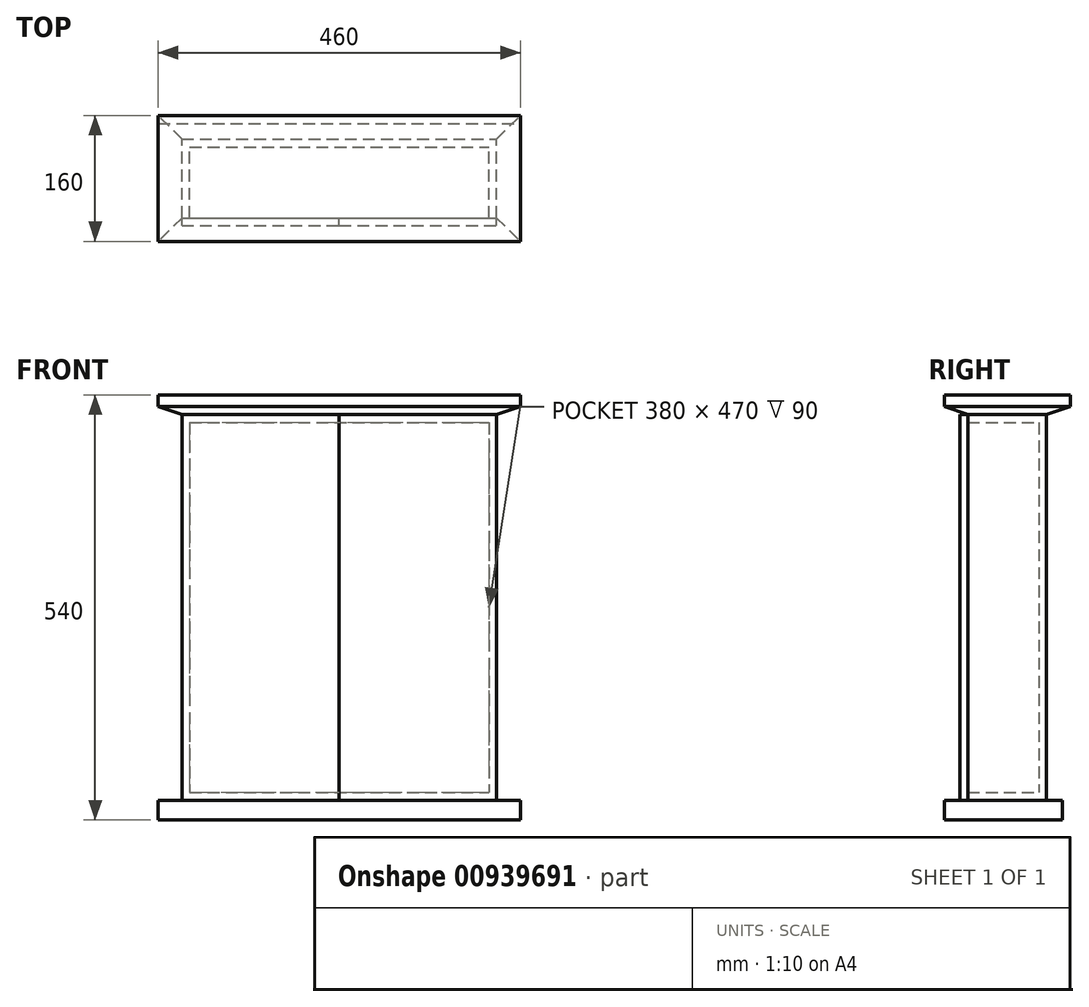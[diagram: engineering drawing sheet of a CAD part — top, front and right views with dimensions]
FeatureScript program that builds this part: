
annotation { "Feature Type Name" : "Feature", "Feature Type Description" : "" }
export const myFeature = defineFeature(function(context is Context, id is Id, definition is map)
    precondition{}
    {
        {
            var Q0;
            Q0=qCreatedBy(makeId("Front.planeOp"),FACE);
            var sketch = newSketch(context, id + "F0", { "sketchPlane" : qUnion([Q0])});
            skLineSegment(sketch, "E0.bottom", {"start": v(-200, 336.12) * mm, "end": v(200, 336.12) * mm});
            skLineSegment(sketch, "E0.top", {"start": v(-200, -153.88) * mm, "end": v(200, -153.88) * mm});
            skLineSegment(sketch, "E0.left", {"start": v(-200, 336.12) * mm, "end": v(-200, -153.88) * mm});
            skLineSegment(sketch, "E0.right", {"start": v(200, 336.12) * mm, "end": v(200, -153.88) * mm});
            skSolve(sketch);
        }
        {
            var Q0;
            Q0 = qSketchRegion(id + "F0", true);
            extrude(context, id + "F1", {"entities" : qUnion([Q0]), "depth" : 100 * mm, "offsetDistance" : 25 * mm});
        }
        {
            var Q0;
            Q0=makeQuery(id+"F1.opExtrude","CAP_FACE",FACE,{"disambiguationData":[OSD([sQuery(id+"F0.wireOp",EDGE,"E0.bottom"),sQuery(id+"F0.wireOp",EDGE,"E0.top"),sQuery(id+"F0.wireOp",EDGE,"E0.left"),sQuery(id+"F0.wireOp",EDGE,"E0.right")])],"isStart":false});
            shell(context, id + "F2", {"entities" : qUnion([Q0]), "thickness" : 10 * mm});
        }
        {
            var Q0;
            Q0=makeQuery(id+"F1.opExtrude","SWEPT_FACE",FACE,{"disambiguationData":[OSD([sQuery(id+"F0.wireOp",EDGE,"E0.bottom")])]});
            var sketch = newSketch(context, id + "F3", { "sketchPlane" : qUnion([Q0])});
            skLineSegment(sketch, "E1.bottom", {"start": v(-230, 30) * mm, "end": v(230, 30) * mm});
            skLineSegment(sketch, "E1.top", {"start": v(-230, -130) * mm, "end": v(230, -130) * mm});
            skLineSegment(sketch, "E1.left", {"start": v(-230, 30) * mm, "end": v(-230, -130) * mm});
            skLineSegment(sketch, "E1.right", {"start": v(230, 30) * mm, "end": v(230, -130) * mm});
            skSolve(sketch);
        }
        {
            var Q0;
            Q0 = qSketchRegion(id + "F3", true);
            extrude(context, id + "F4", {"entities" : qUnion([Q0]), "depth" : 25 * mm, "offsetDistance" : 25 * mm, "hasSecondDirection" : true, "secondDirectionOppositeDirection" : false, "secondDirectionDepth" : 10 * mm});
        }
        {
            var Q1;
            Q1=makeQuery(id+"F1.opExtrude","SWEPT_FACE",FACE,{"disambiguationData":[OSD([sQuery(id+"F0.wireOp",EDGE,"E0.bottom")])]});
            var Q2;
            Q2=makeQuery(id+"F4.opExtrude","CAP_FACE",FACE,{"disambiguationData":[OSD([sQuery(id+"F3.wireOp",EDGE,"E1.bottom"),sQuery(id+"F3.wireOp",EDGE,"E1.top"),sQuery(id+"F3.wireOp",EDGE,"E1.left"),sQuery(id+"F3.wireOp",EDGE,"E1.right")])],"isStart":true});
            loft(context, id + "F5", {"operationType" : NewBodyOperationType.ADD, "sheetProfilesArray" : [{ "sheetProfileEntities" : qUnion([Q1]) }, { "sheetProfileEntities" : qUnion([Q2]) }]});
        }
        {
            var Q0;
            Q0=makeQuery(id+"F1.opExtrude","SWEPT_FACE",FACE,{"disambiguationData":[OSD([sQuery(id+"F0.wireOp",EDGE,"E0.top")])]});
            var sketch = newSketch(context, id + "F6", { "sketchPlane" : qUnion([Q0])});
            skLineSegment(sketch, "E2.bottom", {"start": v(-230, 130) * mm, "end": v(230, 130) * mm});
            skLineSegment(sketch, "E2.top", {"start": v(-230, -20) * mm, "end": v(230, -20) * mm});
            skLineSegment(sketch, "E2.left", {"start": v(-230, 130) * mm, "end": v(-230, -20) * mm});
            skLineSegment(sketch, "E2.right", {"start": v(230, 130) * mm, "end": v(230, -20) * mm});
            skSolve(sketch);
        }
        {
            var Q0;
            Q0=makeQuery(id+"F6.imprint","IMPRINT",FACE,{"disambiguationData":[TD([[makeQuery(id+"F6.imprint","IMPRINT",EDGE,{"derivedFrom":sQuery(id+"F6.wireOp",EDGE,"E2.bottom")}),-1.0]])]});
            var Q1;
            {var subQ0=sQuery(id+"F0.wireOp",EDGE,"E0.top");Q1=makeQuery(id+"F6.imprint","IMPRINT",FACE,{"disambiguationData":[TD([[makeQuery(id+"F6.imprint","IMPRINT",EDGE,{"derivedFrom":makeQuery(id+"F1.opExtrude","CAP_EDGE",EDGE,{"disambiguationData":[OSD([subQ0])],"isStart":true})}),1.0]])]});}
            extrude(context, id + "F7", {"entities" : qUnion([Q0, Q1]), "operationType" : NewBodyOperationType.ADD, "depth" : 25 * mm, "offsetDistance" : 25 * mm});
        }
        {
            var Q0;
            Q0=makeQuery(id+"F1.opExtrude","CAP_FACE",FACE,{"disambiguationData":[OSD([sQuery(id+"F0.wireOp",EDGE,"E0.bottom"),sQuery(id+"F0.wireOp",EDGE,"E0.top"),sQuery(id+"F0.wireOp",EDGE,"E0.left"),sQuery(id+"F0.wireOp",EDGE,"E0.right")])],"isStart":false});
            var sketch = newSketch(context, id + "F8", { "sketchPlane" : qUnion([Q0])});
            skLineSegment(sketch, "E3.bottom", {"start": v(0, 336.12) * mm, "end": v(200, 336.12) * mm});
            skLineSegment(sketch, "E3.top", {"start": v(0, -153.88) * mm, "end": v(200, -153.88) * mm});
            skLineSegment(sketch, "E3.left", {"start": v(0, 336.12) * mm, "end": v(0, -153.88) * mm});
            skLineSegment(sketch, "E3.right", {"start": v(200, 336.12) * mm, "end": v(200, -153.88) * mm});
            skLineSegment(sketch, "E4.bottom", {"start": v(0, 336.12) * mm, "end": v(-200, 336.12) * mm});
            skLineSegment(sketch, "E4.top", {"start": v(0, -153.88) * mm, "end": v(-200, -153.88) * mm});
            skLineSegment(sketch, "E4.right", {"start": v(-200, 336.12) * mm, "end": v(-200, -153.88) * mm});
            skSolve(sketch);
        }
        {
            var Q0;
            {var subQ7=sQuery(id+"F8.wireOp",EDGE,"E3.bottom");Q0=makeQuery(id+"F8.imprint","IMPRINT",FACE,{"disambiguationData":[TD([[makeQuery(id+"F8.imprint","IMPRINT",EDGE,{"derivedFrom":subQ7}),-1.0]])]});}
            var Q1;
            {var subQ7=sQuery(id+"F0.wireOp",EDGE,"E0.right");var subQ8=makeQuery(id+"F2.opShell","OFFSET_EDGE",EDGE,{"disambiguationData":[OSD([subQ7]),TDD([makeQuery(id+"F1.opExtrude","CAP_EDGE",EDGE,{"disambiguationData":[OSD([subQ7])],"isStart":false})])]});Q1=makeQuery(id+"F8.imprint","IMPRINT",FACE,{"disambiguationData":[TD([[makeQuery(id+"F8.imprint","IMPRINT",EDGE,{"derivedFrom":subQ8}),-1.0]])]});}
            extrude(context, id + "F9", {"entities" : qUnion([Q0, Q1]), "depth" : 10 * mm, "offsetDistance" : 25 * mm});
        }
        {
            var Q0;
            {var subQ7=sQuery(id+"F0.wireOp",EDGE,"E0.left");var subQ8=makeQuery(id+"F2.opShell","OFFSET_EDGE",EDGE,{"disambiguationData":[OSD([subQ7]),TDD([makeQuery(id+"F1.opExtrude","CAP_EDGE",EDGE,{"disambiguationData":[OSD([subQ7])],"isStart":false})])]});Q0=makeQuery(id+"F8.imprint","IMPRINT",FACE,{"disambiguationData":[TD([[makeQuery(id+"F8.imprint","IMPRINT",EDGE,{"derivedFrom":subQ8}),1.0]])]});}
            var Q1;
            {var subQ5=sQuery(id+"F8.wireOp",EDGE,"E4.bottom");Q1=makeQuery(id+"F8.imprint","IMPRINT",FACE,{"disambiguationData":[TD([[makeQuery(id+"F8.imprint","IMPRINT",EDGE,{"derivedFrom":subQ5}),-1.0]])]});}
            extrude(context, id + "F10", {"entities" : qUnion([Q0, Q1]), "depth" : 10 * mm, "offsetDistance" : 25 * mm});
        }
    });
